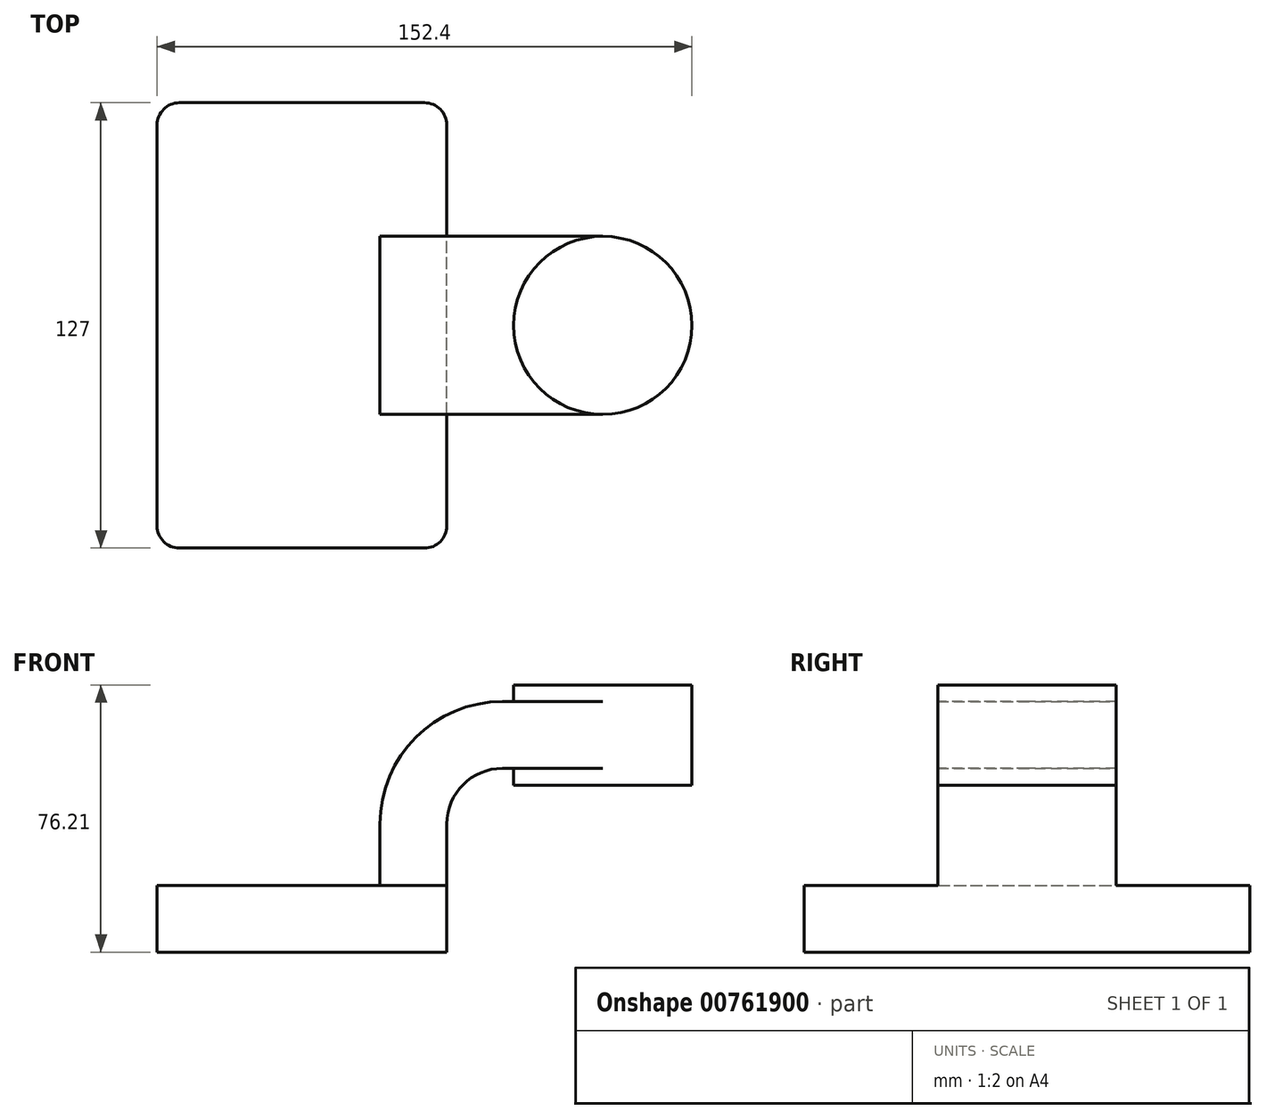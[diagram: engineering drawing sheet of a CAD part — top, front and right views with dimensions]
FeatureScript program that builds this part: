
annotation { "Feature Type Name" : "Feature", "Feature Type Description" : "" }
export const myFeature = defineFeature(function(context is Context, id is Id, definition is map)
    precondition{}
    {
        {
            var Q0;
            Q0=qCreatedBy(makeId("Front.planeOp"),FACE);
            var sketch = newSketch(context, id + "F0", { "sketchPlane" : qUnion([Q0])});
            skLineSegment(sketch, "E0.bottom", {"start": v(41.28, -9.52) * mm, "end": v(-41.28, -9.53) * mm});
            skLineSegment(sketch, "E0.top", {"start": v(41.28, 9.53) * mm, "end": v(-41.28, 9.53) * mm});
            skLineSegment(sketch, "E0.left", {"start": v(41.28, -9.52) * mm, "end": v(41.28, 9.53) * mm});
            skLineSegment(sketch, "E0.right", {"start": v(-41.28, -9.53) * mm, "end": v(-41.28, 9.53) * mm});
            skPoint(sketch, "E0.middle", {"position": v(0, 0) * mm});
            skLineSegment(sketch, "E1.bottom", {"start": v(111.12, 38.1) * mm, "end": v(60.33, 38.1) * mm});
            skLineSegment(sketch, "E1.top", {"start": v(111.12, 66.68) * mm, "end": v(60.33, 66.68) * mm});
            skLineSegment(sketch, "E1.left", {"start": v(111.13, 38.1) * mm, "end": v(111.13, 66.68) * mm});
            skLineSegment(sketch, "E1.right", {"start": v(60.33, 38.1) * mm, "end": v(60.33, 66.68) * mm});
            skPoint(sketch, "E1.middle", {"position": v(85.72, 52.39) * mm});
            skLineSegment(sketch, "E2", {"start": v(41.27, 9.53) * mm, "end": v(41.27, 27) * mm});
            skArc(sketch, "E3", {"start": v(41.27, 27) * mm, "mid": v(45.92, 38.23) * mm, "end": v(57.15, 42.88) * mm});
            skLineSegment(sketch, "E4", {"start": v(57.15, 42.88) * mm, "end": v(85.72, 42.88) * mm});
            skLineSegment(sketch, "E5.0", {"start": v(57.15, 61.93) * mm, "end": v(85.72, 61.93) * mm});
            skArc(sketch, "E5.1", {"start": v(22.23, 27) * mm, "mid": v(32.45, 51.7) * mm, "end": v(57.15, 61.93) * mm});
            skLineSegment(sketch, "E5.2", {"start": v(22.22, 9.53) * mm, "end": v(22.22, 27) * mm});
            skLineSegment(sketch, "E6", {"start": v(85.73, 38.1) * mm, "end": v(85.73, 66.68) * mm});
            skFitSpline(sketch, "E7", {"points": [v(-41.28, 9.53) * mm, v(57.15, 61.93) * mm], "startDerivative": vector(0, 84.48) * mm, "endDerivative": vector(103.3, 0) * mm});
            skSolve(sketch);
        }
        {
            var Q0;
            Q0=makeQuery(id+"F0.imprint","IMPRINT",FACE,{"disambiguationData":[TD([[makeQuery(id+"F0.imprint","IMPRINT",EDGE,{"derivedFrom":sQuery(id+"F0.wireOp",EDGE,"E0.bottom")}),-1.0]])]});
            extrude(context, id + "F1", {"entities" : qUnion([Q0]), "endBound" : BoundingType.SYMMETRIC, "depth" : 127 * mm, "offsetDistance" : 25.4 * mm});
        }
        {
            var Q0;
            {var subQ1=sQuery(id+"F0.wireOp",EDGE,"E2");Q0=makeQuery(id+"F0.imprint","IMPRINT",FACE,{"disambiguationData":[TD([[makeQuery(id+"F0.imprint","IMPRINT",EDGE,{"derivedFrom":subQ1}),1.0]])]});}
            var Q1;
            {var subQ0=sQuery(id+"F0.wireOp",EDGE,"E4");var subQ1=sQuery(id+"F0.wireOp",EDGE,"E1.right");var subQ2=makeQuery(id+"F0.imprint","INTERSECT",VERTEX,{"derivedFrom":[subQ1,subQ0]});Q1=makeQuery(id+"F0.imprint","IMPRINT",FACE,{"disambiguationData":[TD([[makeQuery(id+"F0.imprint","IMPRINT",EDGE,{"disambiguationData":[TD([[subQ2,-1.0]])],"derivedFrom":subQ1}),-1.0]])]});}
            extrude(context, id + "F2", {"entities" : qUnion([Q0, Q1]), "operationType" : NewBodyOperationType.ADD, "endBound" : BoundingType.SYMMETRIC, "depth" : 50.8 * mm, "offsetDistance" : 25.4 * mm});
        }
        {
            var Q0;
            Q0=makeQuery(id+"F0.imprint","IMPRINT",FACE,{"disambiguationData":[TD([[makeQuery(id+"F0.imprint","IMPRINT",EDGE,{"derivedFrom":sQuery(id+"F0.wireOp",EDGE,"E5.1")}),1.0]])]});
            extrude(context, id + "F3", {"entities" : qUnion([Q0]), "operationType" : NewBodyOperationType.ADD, "endBound" : BoundingType.SYMMETRIC, "depth" : 15.88 * mm, "offsetDistance" : 25.4 * mm});
        }
        {
            var Q0;
            {var subQ4=sQuery(id+"F0.wireOp",EDGE,"E1.left");Q0=makeQuery(id+"F0.imprint","IMPRINT",FACE,{"disambiguationData":[TD([[makeQuery(id+"F0.imprint","IMPRINT",EDGE,{"derivedFrom":subQ4}),1.0]])]});}
            var Q1;
            Q1=sQuery(id+"F0.wireOp",EDGE,"E6");
            revolve(context, id + "F4", {"operationType" : NewBodyOperationType.ADD, "surfaceOperationType" : NewSurfaceOperationType.NEW, "entities" : qUnion([Q0]), "axis" : qUnion([Q1]), "revolveType" : RevolveType.FULL});
        }
        {
            var Q0;
            Q0=makeQuery(id+"F1.opExtrude","CAP_EDGE",EDGE,{"disambiguationData":[OSD([sQuery(id+"F0.wireOp",EDGE,"E0.right")])],"isStart":false});
            var Q1;
            Q1=makeQuery(id+"F1.opExtrude","CAP_EDGE",EDGE,{"disambiguationData":[OSD([sQuery(id+"F0.wireOp",EDGE,"E0.left")])],"isStart":false});
            var Q2;
            Q2=makeQuery(id+"F1.opExtrude","CAP_EDGE",EDGE,{"disambiguationData":[OSD([sQuery(id+"F0.wireOp",EDGE,"E0.left")])],"isStart":true});
            var Q3;
            Q3=makeQuery(id+"F1.opExtrude","CAP_EDGE",EDGE,{"disambiguationData":[OSD([sQuery(id+"F0.wireOp",EDGE,"E0.right")])],"isStart":true});
            fillet(context, id + "F5", {"entities" : qUnion([Q0, Q1, Q2, Q3]), "radius" : 6.35 * mm, "tangentPropagation" : true, "allowEdgeOverflow" : false});
        }
    });
